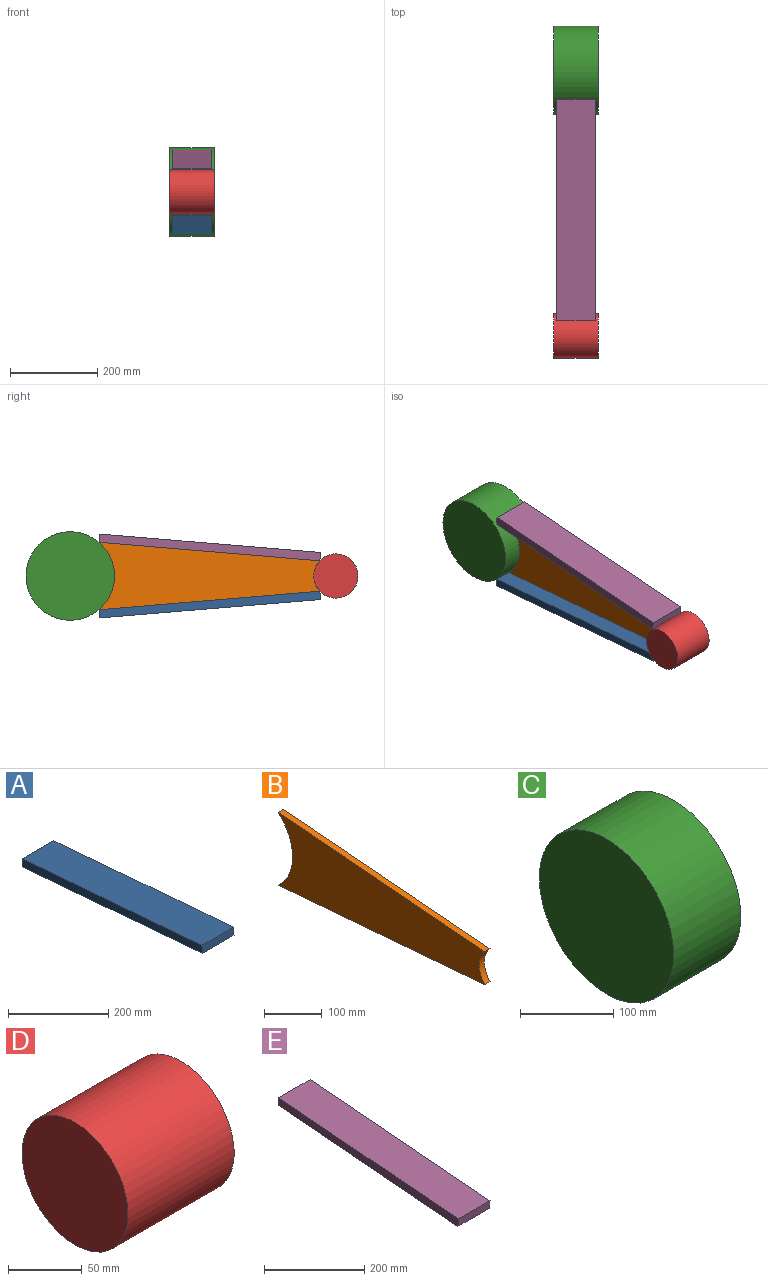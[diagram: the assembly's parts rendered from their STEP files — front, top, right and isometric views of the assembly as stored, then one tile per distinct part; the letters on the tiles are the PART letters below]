
ASSEMBLY  parts=5 mates=4
PART A: 6 faces, bbox 88.9x508.4x61.4 mm
  f0: plane 506.83x88.9mm, normal (0,0.08,1), area 45214.1mm2, adj f1,f3,f4,f5
  f1: plane 88.9x18.98mm, normal (0,-1,0.08), area 1693.5mm2, adj f0,f2,f4,f5
  f2: plane 506.83x88.9mm, normal (0,-0.08,-1), area 45214.1mm2, adj f1,f3,f4,f5
  f3: plane 88.9x18.98mm, normal (0,1,-0.08), area 1693.5mm2, adj f0,f2,f4,f5
  f4: plane 508.41x61.37mm, normal (1,0,0), area 9688.7mm2, adj f0,f1,f2,f3
  f5: plane 508.41x61.37mm, normal (-1,0,0), area 9688.7mm2, adj f0,f1,f2,f3
PART B: 6 faces, bbox 12.7x506.8x154.7 mm
  f0: cylinder r=101.6mm len=154.65mm, axis (-1,0,0), area 2232.2mm2, adj f1,f3,f4,f5
  f1: plane 506.83x42.38mm, normal (0,-0.08,1), area 6459.2mm2, adj f0,f2,f4,f5
  f2: cylinder r=50.8mm len=69.89mm, axis (-1,0,0), area 978.8mm2, adj f1,f3,f4,f5
  f3: plane 506.83x42.38mm, normal (0,-0.08,-1), area 6459.2mm2, adj f0,f2,f4,f5
  f4: plane 506.83x154.65mm, normal (1,0,0), area 52399.9mm2, adj f0,f1,f2,f3
  f5: plane 506.83x154.65mm, normal (-1,0,0), area 52399.9mm2, adj f0,f1,f2,f3
PART C: 3 faces, bbox 101.6x203.2x203.2 mm
  f0: cylinder r=101.6mm len=203.2mm, axis (-1,0,0), area 64858.6mm2, adj f1,f2
  f1: plane 203.2x203.2mm, normal (1,0,0), area 32429.3mm2, adj f0
  f2: plane 203.2x203.2mm, normal (-1,0,0), area 32429.3mm2, adj f0
PART D: 3 faces, bbox 101.6x101.6x101.6 mm
  f0: cylinder r=50.8mm len=101.6mm, axis (-1,0,0), area 32429.3mm2, adj f1,f2
  f1: plane 101.6x101.6mm, normal (1,0,0), area 8107.3mm2, adj f0
  f2: plane 101.6x101.6mm, normal (-1,0,0), area 8107.3mm2, adj f0
PART E: 6 faces, bbox 88.9x508.4x61.4 mm
  f0: plane 88.9x18.98mm, normal (0,-1,-0.08), area 1693.5mm2, adj f1,f3,f4,f5
  f1: plane 506.83x88.9mm, normal (0,0.08,-1), area 45214.1mm2, adj f0,f2,f4,f5
  f2: plane 88.9x18.98mm, normal (0,1,0.08), area 1693.5mm2, adj f1,f3,f4,f5
  f3: plane 506.83x88.9mm, normal (0,-0.08,1), area 45214.1mm2, adj f0,f2,f4,f5
  f4: plane 508.41x61.37mm, normal (1,0,0), area 9688.7mm2, adj f0,f1,f2,f3
  f5: plane 508.41x61.37mm, normal (-1,0,0), area 9688.7mm2, adj f0,f1,f2,f3
PLACE A t=(-122.06,136.54,-60.72)mm
PLACE B t=(-122.06,136.54,-60.72)mm
PLACE C t=(-122.06,136.54,-60.72)mm fixed
PLACE D t=(-122.06,136.54,-60.72)mm
PLACE E t=(-122.06,136.54,-60.72)mm
MATE fastened D.f0 <-> B.f2  axis (-1,0,0) through (-122.06,-473.06,-60.72)mm
MATE fastened B.f3 <-> A.f0  axis (0,-0.08,-1) through (-122.06,-182.77,-116.85)mm
MATE fastened E.f1 <-> B.f1  axis (0,0.08,-1) through (-122.06,-182.77,-4.58)mm
MATE fastened C.f0 <-> B.f0  axis (-1,0,0) through (-122.06,136.54,-60.72)mm
